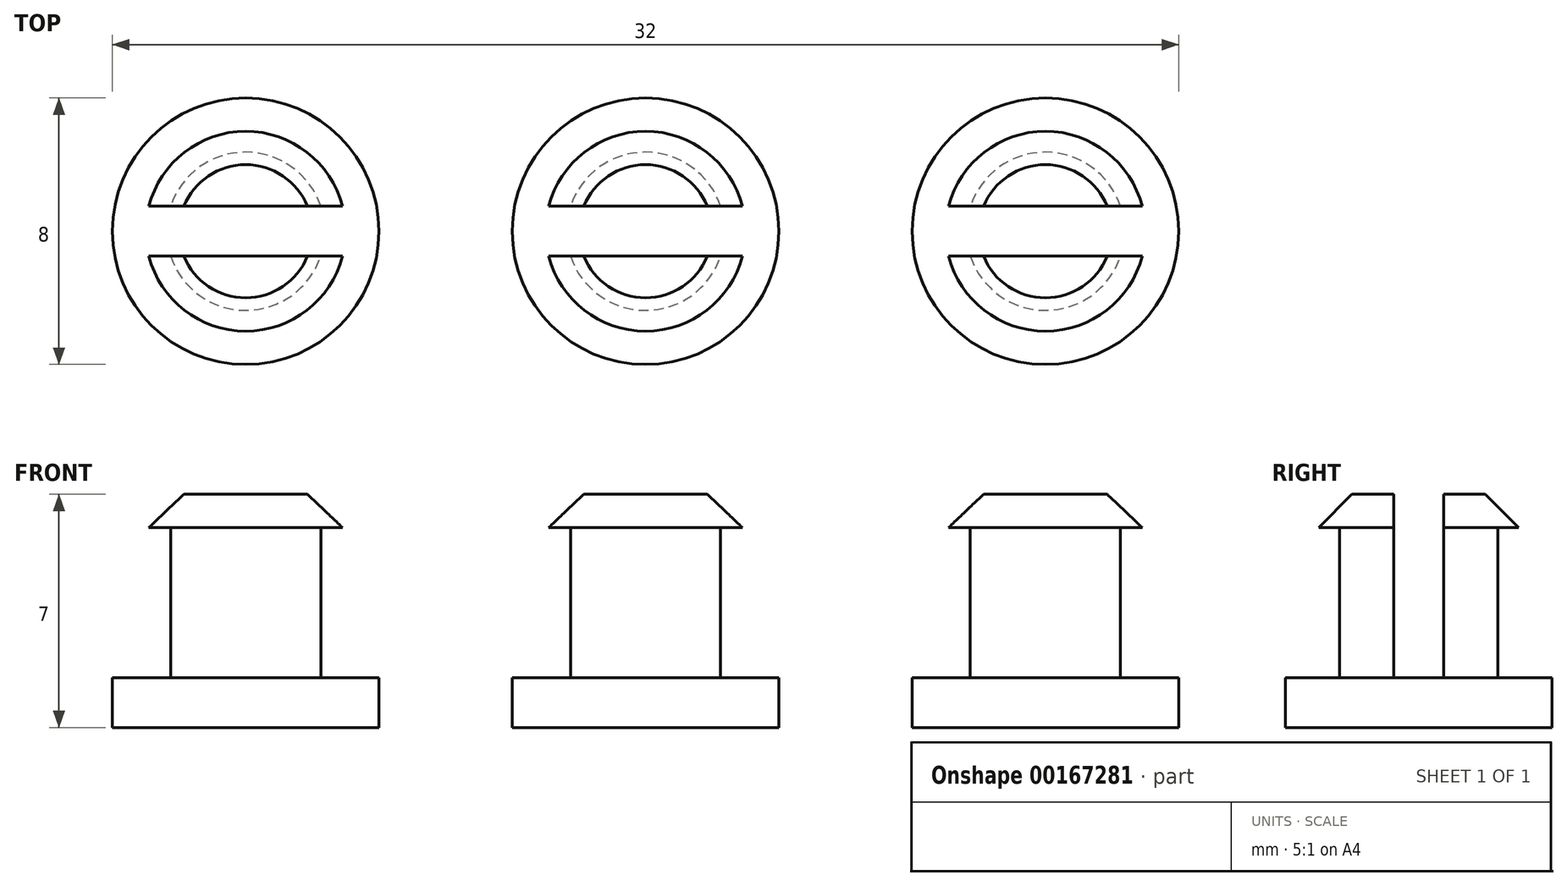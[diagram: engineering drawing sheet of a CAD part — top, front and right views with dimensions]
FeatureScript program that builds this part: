
annotation { "Feature Type Name" : "Feature", "Feature Type Description" : "" }
export const myFeature = defineFeature(function(context is Context, id is Id, definition is map)
    precondition{}
    {
        {
            var Q0;
            Q0=qCreatedBy(makeId("Top.planeOp"),FACE);
            var sketch = newSketch(context, id + "F0", { "sketchPlane" : qUnion([Q0])});
            skCircle(sketch, "E0", {"center": v(0, 0) * mm, "radius": 4 * mm});
            skCircle(sketch, "E1", {"center": v(0, 0) * mm, "radius": 2.38 * mm});
            skLineSegment(sketch, "E2.bottom", {"start": v(-3.5, 0.75) * mm, "end": v(3.5, 0.75) * mm});
            skLineSegment(sketch, "E2.top", {"start": v(-3.5, -0.75) * mm, "end": v(3.5, -0.75) * mm});
            skLineSegment(sketch, "E2.left", {"start": v(-3.5, 0.75) * mm, "end": v(-3.5, -0.75) * mm});
            skLineSegment(sketch, "E2.right", {"start": v(3.5, 0.75) * mm, "end": v(3.5, -0.75) * mm});
            skCircle(sketch, "E3", {"center": v(0, 0) * mm, "radius": 3 * mm});
            skSolve(sketch);
        }
        {
            var Q0;
            {var subQ0=sQuery(id+"F0.wireOp",EDGE,"E2.bottom");var subQ1=sQuery(id+"F0.wireOp",EDGE,"E1");var subQ2=makeQuery(id+"F0.imprint","INTERSECT",VERTEX,{"disambiguationData":[OD(0.0)],"derivedFrom":[subQ1,subQ0]});Q0=makeQuery(id+"F0.imprint","IMPRINT",FACE,{"disambiguationData":[TD([[makeQuery(id+"F0.imprint","IMPRINT",EDGE,{"disambiguationData":[TD([[subQ2,-1.0]])],"derivedFrom":subQ1}),1.0]])]});}
            var Q1;
            {var subQ5=sQuery(id+"F0.wireOp",EDGE,"E2.right");Q1=makeQuery(id+"F0.imprint","IMPRINT",FACE,{"disambiguationData":[TD([[makeQuery(id+"F0.imprint","IMPRINT",EDGE,{"derivedFrom":subQ5}),-1.0]])]});}
            var Q2;
            {var subQ5=sQuery(id+"F0.wireOp",EDGE,"E2.left");Q2=makeQuery(id+"F0.imprint","IMPRINT",FACE,{"disambiguationData":[TD([[makeQuery(id+"F0.imprint","IMPRINT",EDGE,{"derivedFrom":subQ5}),1.0]])]});}
            var Q3;
            {var subQ0=sQuery(id+"F0.wireOp",EDGE,"E2.top");var subQ1=sQuery(id+"F0.wireOp",EDGE,"E1");var subQ2=makeQuery(id+"F0.imprint","INTERSECT",VERTEX,{"disambiguationData":[OD(0.0)],"derivedFrom":[subQ1,subQ0]});Q3=makeQuery(id+"F0.imprint","IMPRINT",FACE,{"disambiguationData":[TD([[makeQuery(id+"F0.imprint","IMPRINT",EDGE,{"disambiguationData":[TD([[subQ2,-1.0]])],"derivedFrom":subQ1}),1.0]])]});}
            var Q4;
            Q4=makeQuery(id+"F0.imprint","IMPRINT",FACE,{"disambiguationData":[TD([[makeQuery(id+"F0.imprint","IMPRINT",EDGE,{"derivedFrom":sQuery(id+"F0.wireOp",EDGE,"E0")}),1.0]])]});
            var Q5;
            {var subQ0=sQuery(id+"F0.wireOp",EDGE,"E2.bottom");var subQ1=sQuery(id+"F0.wireOp",EDGE,"E1");var subQ2=makeQuery(id+"F0.imprint","INTERSECT",VERTEX,{"disambiguationData":[OD(0.0)],"derivedFrom":[subQ1,subQ0]});Q5=makeQuery(id+"F0.imprint","IMPRINT",FACE,{"disambiguationData":[TD([[makeQuery(id+"F0.imprint","IMPRINT",EDGE,{"disambiguationData":[TD([[subQ2,1.0]])],"derivedFrom":subQ1}),1.0]])]});}
            var Q6;
            {var subQ1=sQuery(id+"F0.wireOp",EDGE,"E1");var subQ5=sQuery(id+"F0.wireOp",EDGE,"E2.bottom");var subQ8=makeQuery(id+"F0.imprint","INTERSECT",VERTEX,{"disambiguationData":[OD(0.0)],"derivedFrom":[subQ1,subQ5]});Q6=makeQuery(id+"F0.imprint","IMPRINT",FACE,{"disambiguationData":[TD([[makeQuery(id+"F0.imprint","IMPRINT",EDGE,{"disambiguationData":[TD([[subQ8,-1.0]])],"derivedFrom":subQ1}),-1.0]])]});}
            var Q7;
            {var subQ0=sQuery(id+"F0.wireOp",EDGE,"E2.top");var subQ1=sQuery(id+"F0.wireOp",EDGE,"E1");var subQ2=makeQuery(id+"F0.imprint","INTERSECT",VERTEX,{"disambiguationData":[OD(0.0)],"derivedFrom":[subQ1,subQ0]});Q7=makeQuery(id+"F0.imprint","IMPRINT",FACE,{"disambiguationData":[TD([[makeQuery(id+"F0.imprint","IMPRINT",EDGE,{"disambiguationData":[TD([[subQ2,-1.0]])],"derivedFrom":subQ1}),-1.0]])]});}
            var Q8;
            {var subQ1=sQuery(id+"F0.wireOp",EDGE,"E1");var subQ6=sQuery(id+"F0.wireOp",EDGE,"E2.bottom");var subQ7=makeQuery(id+"F0.imprint","INTERSECT",VERTEX,{"disambiguationData":[OD(1.0)],"derivedFrom":[subQ1,subQ6]});Q8=makeQuery(id+"F0.imprint","IMPRINT",FACE,{"disambiguationData":[TD([[makeQuery(id+"F0.imprint","IMPRINT",EDGE,{"disambiguationData":[TD([[subQ7,1.0]])],"derivedFrom":subQ1}),-1.0]])]});}
            var Q9;
            {var subQ0=sQuery(id+"F0.wireOp",EDGE,"E2.bottom");var subQ1=sQuery(id+"F0.wireOp",EDGE,"E1");var subQ2=makeQuery(id+"F0.imprint","INTERSECT",VERTEX,{"disambiguationData":[OD(0.0)],"derivedFrom":[subQ1,subQ0]});Q9=makeQuery(id+"F0.imprint","IMPRINT",FACE,{"disambiguationData":[TD([[makeQuery(id+"F0.imprint","IMPRINT",EDGE,{"disambiguationData":[TD([[subQ2,1.0]])],"derivedFrom":subQ1}),-1.0]])]});}
            extrude(context, id + "F1", {"entities" : qUnion([Q0, Q1, Q2, Q3, Q4, Q5, Q6, Q7, Q8, Q9]), "depth" : 1.5 * mm});
        }
        {
            var Q0;
            {var subQ0=sQuery(id+"F0.wireOp",EDGE,"E2.bottom");var subQ1=sQuery(id+"F0.wireOp",EDGE,"E1");var subQ2=makeQuery(id+"F0.imprint","INTERSECT",VERTEX,{"disambiguationData":[OD(0.0)],"derivedFrom":[subQ1,subQ0]});Q0=makeQuery(id+"F0.imprint","IMPRINT",FACE,{"disambiguationData":[TD([[makeQuery(id+"F0.imprint","IMPRINT",EDGE,{"disambiguationData":[TD([[subQ2,1.0]])],"derivedFrom":subQ1}),1.0]])]});}
            var Q1;
            {var subQ0=sQuery(id+"F0.wireOp",EDGE,"E2.top");var subQ1=sQuery(id+"F0.wireOp",EDGE,"E1");var subQ2=makeQuery(id+"F0.imprint","INTERSECT",VERTEX,{"disambiguationData":[OD(0.0)],"derivedFrom":[subQ1,subQ0]});Q1=makeQuery(id+"F0.imprint","IMPRINT",FACE,{"disambiguationData":[TD([[makeQuery(id+"F0.imprint","IMPRINT",EDGE,{"disambiguationData":[TD([[subQ2,-1.0]])],"derivedFrom":subQ1}),1.0]])]});}
            extrude(context, id + "F2", {"entities" : qUnion([Q0, Q1]), "operationType" : NewBodyOperationType.ADD, "depth" : 6.5 * mm});
        }
        {
            var Q0;
            {var subQ0=sQuery(id+"F0.wireOp",EDGE,"E2.top");var subQ1=sQuery(id+"F0.wireOp",EDGE,"E1");var subQ2=makeQuery(id+"F0.imprint","INTERSECT",VERTEX,{"disambiguationData":[OD(0.0)],"derivedFrom":[subQ1,subQ0]});Q0=makeQuery(id+"F0.imprint","IMPRINT",FACE,{"disambiguationData":[TD([[makeQuery(id+"F0.imprint","IMPRINT",EDGE,{"disambiguationData":[TD([[subQ2,-1.0]])],"derivedFrom":subQ1}),-1.0]])]});}
            var Q1;
            {var subQ0=sQuery(id+"F0.wireOp",EDGE,"E2.bottom");var subQ1=sQuery(id+"F0.wireOp",EDGE,"E1");var subQ2=makeQuery(id+"F0.imprint","INTERSECT",VERTEX,{"disambiguationData":[OD(0.0)],"derivedFrom":[subQ1,subQ0]});Q1=makeQuery(id+"F0.imprint","IMPRINT",FACE,{"disambiguationData":[TD([[makeQuery(id+"F0.imprint","IMPRINT",EDGE,{"disambiguationData":[TD([[subQ2,1.0]])],"derivedFrom":subQ1}),-1.0]])]});}
            var Q2;
            {var subQ0=sQuery(id+"F0.wireOp",EDGE,"E2.bottom");var subQ1=sQuery(id+"F0.wireOp",EDGE,"E1");var subQ2=makeQuery(id+"F0.imprint","INTERSECT",VERTEX,{"disambiguationData":[OD(0.0)],"derivedFrom":[subQ1,subQ0]});Q2=makeQuery(id+"F0.imprint","IMPRINT",FACE,{"disambiguationData":[TD([[makeQuery(id+"F0.imprint","IMPRINT",EDGE,{"disambiguationData":[TD([[subQ2,1.0]])],"derivedFrom":subQ1}),1.0]])]});}
            var Q3;
            {var subQ0=sQuery(id+"F0.wireOp",EDGE,"E2.top");var subQ1=sQuery(id+"F0.wireOp",EDGE,"E1");var subQ2=makeQuery(id+"F0.imprint","INTERSECT",VERTEX,{"disambiguationData":[OD(0.0)],"derivedFrom":[subQ1,subQ0]});Q3=makeQuery(id+"F0.imprint","IMPRINT",FACE,{"disambiguationData":[TD([[makeQuery(id+"F0.imprint","IMPRINT",EDGE,{"disambiguationData":[TD([[subQ2,-1.0]])],"derivedFrom":subQ1}),1.0]])]});}
            extrude(context, id + "F3", {"entities" : qUnion([Q0, Q1, Q2, Q3]), "operationType" : NewBodyOperationType.ADD, "depth" : 7 * mm, "hasSecondDirection" : true, "secondDirectionOppositeDirection" : false, "secondDirectionDepth" : 6 * mm});
        }
        {
            var Q0;
            {var subQ0=sQuery(id+"F0.wireOp",EDGE,"E3");var subQ1=sQuery(id+"F0.wireOp",EDGE,"E2.bottom");Q0=makeQuery(id+"F3.opExtrude","CAP_EDGE",EDGE,{"disambiguationData":[OSD([subQ0]),TDD([makeQuery(id+"F0.imprint","IMPRINT",EDGE,{"disambiguationData":[TD([[makeQuery(id+"F0.imprint","INTERSECT",VERTEX,{"disambiguationData":[OD(0.0)],"derivedFrom":[subQ1,subQ0]}),1.0]])],"derivedFrom":subQ0})])],"isStart":false});}
            var Q1;
            {var subQ0=sQuery(id+"F0.wireOp",EDGE,"E3");var subQ1=sQuery(id+"F0.wireOp",EDGE,"E2.top");Q1=makeQuery(id+"F3.opExtrude","CAP_EDGE",EDGE,{"disambiguationData":[OSD([subQ0]),TDD([makeQuery(id+"F0.imprint","IMPRINT",EDGE,{"disambiguationData":[TD([[makeQuery(id+"F0.imprint","INTERSECT",VERTEX,{"disambiguationData":[OD(0.0)],"derivedFrom":[subQ1,subQ0]}),-1.0]])],"derivedFrom":subQ0})])],"isStart":false});}
            chamfer(context, id + "F4", {"entities" : qUnion([Q0, Q1]), "width" : 1 * mm, "tangentPropagation" : true});
        }
        {
            var Q0;
            Q0=makeQuery(id+"F1.opExtrude","SWEPT_BODY",BODY,{"disambiguationData":[OSD([sQuery(id+"F0.wireOp",EDGE,"E0")])]});
            transform(context, id + "F5", {"entities" : qUnion([Q0]), "transformType" : TransformType.TRANSLATION_3D, "dx" : 12 * mm, "dy" : 0 * mm, "dz" : 0 * mm, "makeCopy" : true});
        }
        {
            var Q0;
            Q0=makeQuery(id+"F1.opExtrude","SWEPT_BODY",BODY,{"disambiguationData":[OSD([sQuery(id+"F0.wireOp",EDGE,"E0")])]});
            transform(context, id + "F6", {"entities" : qUnion([Q0]), "transformType" : TransformType.TRANSLATION_3D, "dx" : 24 * mm, "dy" : 0 * mm, "dz" : 0 * mm, "makeCopy" : true});
        }
    });
